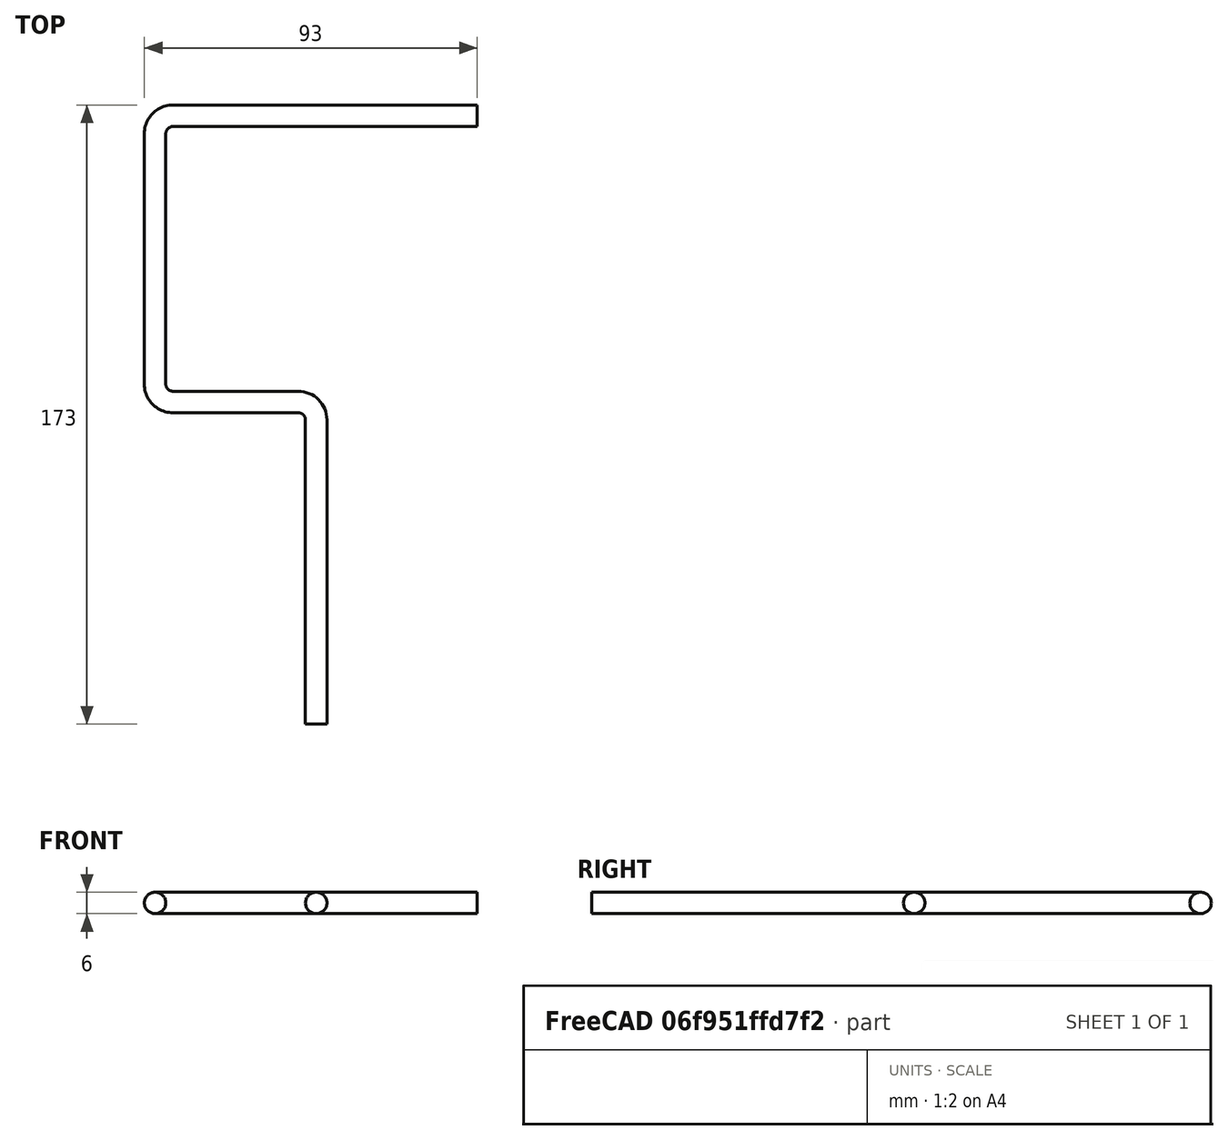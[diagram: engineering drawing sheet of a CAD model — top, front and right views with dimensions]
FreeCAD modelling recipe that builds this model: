
FCSTD DOCUMENT  (FreeCAD 0.19R24276 (Git))
Label: paint roller
License: All rights reserved
LicenseURL: http://en.wikipedia.org/wiki/All_rights_reserved
objects: Sketcher::SketchObject×2, PartDesign::AdditivePipe×1, PartDesign::Body×1, PartDesign::CoordinateSystem×1, App::Part×1
note: 6 computed .brp shape members not serialized (recipe doc carries the construction recipe); baked Part::Feature solids carry a one-line shape summary decoded from their .brp

FEATURE [Sketcher::SketchObject] Sketch
  FullyConstrained = true
  MapMode = 5
  Support = -> [XY_Plane]
  sketch-geometry (7):
    g0: LineSegment StartX=0 StartY=0 StartZ=0 EndX=0 EndY=85 EndZ=0
    g1: LineSegment StartX=-5 StartY=90 StartZ=0 EndX=-40 EndY=90 EndZ=0
    g2: LineSegment StartX=-45 StartY=95 StartZ=0 EndX=-45 EndY=165 EndZ=0
    g3: LineSegment StartX=-40 StartY=170 StartZ=0 EndX=45 EndY=170 EndZ=0
    g4: ArcOfCircle CenterX=-5 CenterY=85 CenterZ=0 NormalX=0 NormalY=0 NormalZ=1 AngleXU=0 Radius=5 StartAngle=-9e-16 EndAngle=1.5708
    g5: ArcOfCircle CenterX=-40 CenterY=95 CenterZ=0 NormalX=0 NormalY=0 NormalZ=1 AngleXU=0 Radius=5 StartAngle=3.14159 EndAngle=4.71239
    g6: ArcOfCircle CenterX=-40 CenterY=165 CenterZ=0 NormalX=0 NormalY=0 NormalZ=1 AngleXU=0 Radius=5 StartAngle=1.5708 EndAngle=3.14159
  constraints (18):
    c: Coincident(g0,g-1)
    c: Horizontal(g1)
    c: Vertical(g2)
    c: Horizontal(g3)
    c: Tangent(g0,g4) = -1.5708
    c: Tangent(g1,g4) = -1.5708
    c: Tangent(g1,g5) = 1.5708
    c: Tangent(g2,g5) = 1.5708
    c: Tangent(g2,g6) = 1.5708
    c: Tangent(g3,g6) = 1.5708
    c: Equal(g6,g5)
    c: Equal(g5,g4)
    c: PointOnObject(g0,g-2)
    c: Diameter(g4) = 10
    c: DistanceY(g-1,g1) = 90
    c: DistanceY(g1,g3) = 80
    c: DistanceX(g2,g3) = 90
    c: DistanceX(g2,g-1) = 45
FEATURE [Sketcher::SketchObject] Sketch001
  FullyConstrained = true
  MapMode = 5
  Placement = pos=(0,0,0) rot=(1,0,0;1.5708rad)
  Support = -> [XZ_Plane]
  sketch-geometry (1):
    g0: Circle CenterX=0 CenterY=0 CenterZ=0 NormalX=0 NormalY=0 NormalZ=1 AngleXU=0 Radius=3
  constraints (2):
    c: Coincident(g0,g-1)
    c: Diameter(g0) = 6
FEATURE [PartDesign::AdditivePipe] AdditivePipe
  AuxilleryCurvelinear = true
  AuxillerySpineTangent = false
  Binormal = (0,0,0)
  Mode = 0
  Placement = pos=(0,0,0) rot=(1,0,0;1.5708rad)
  Profile = -> Sketch001
  Refine = true
  Spine = -> Sketch
  SpineTangent = false
  Transformation = 0
  Transition = 0
FEATURE [PartDesign::Body] Body
  Group = -> [Sketch,Sketch001,AdditivePipe]
  Origin = -> Origin
  Tip = -> AdditivePipe
FEATURE [PartDesign::CoordinateSystem] LCS_0
  AttacherType = Attacher::AttachEngine3D
  MapMode = 2
  Support = -> [X_Axis001]
FEATURE [App::Part] PAINT_ROLLER
  Group = -> [LCS_0,Body]
  Origin = -> Origin001
